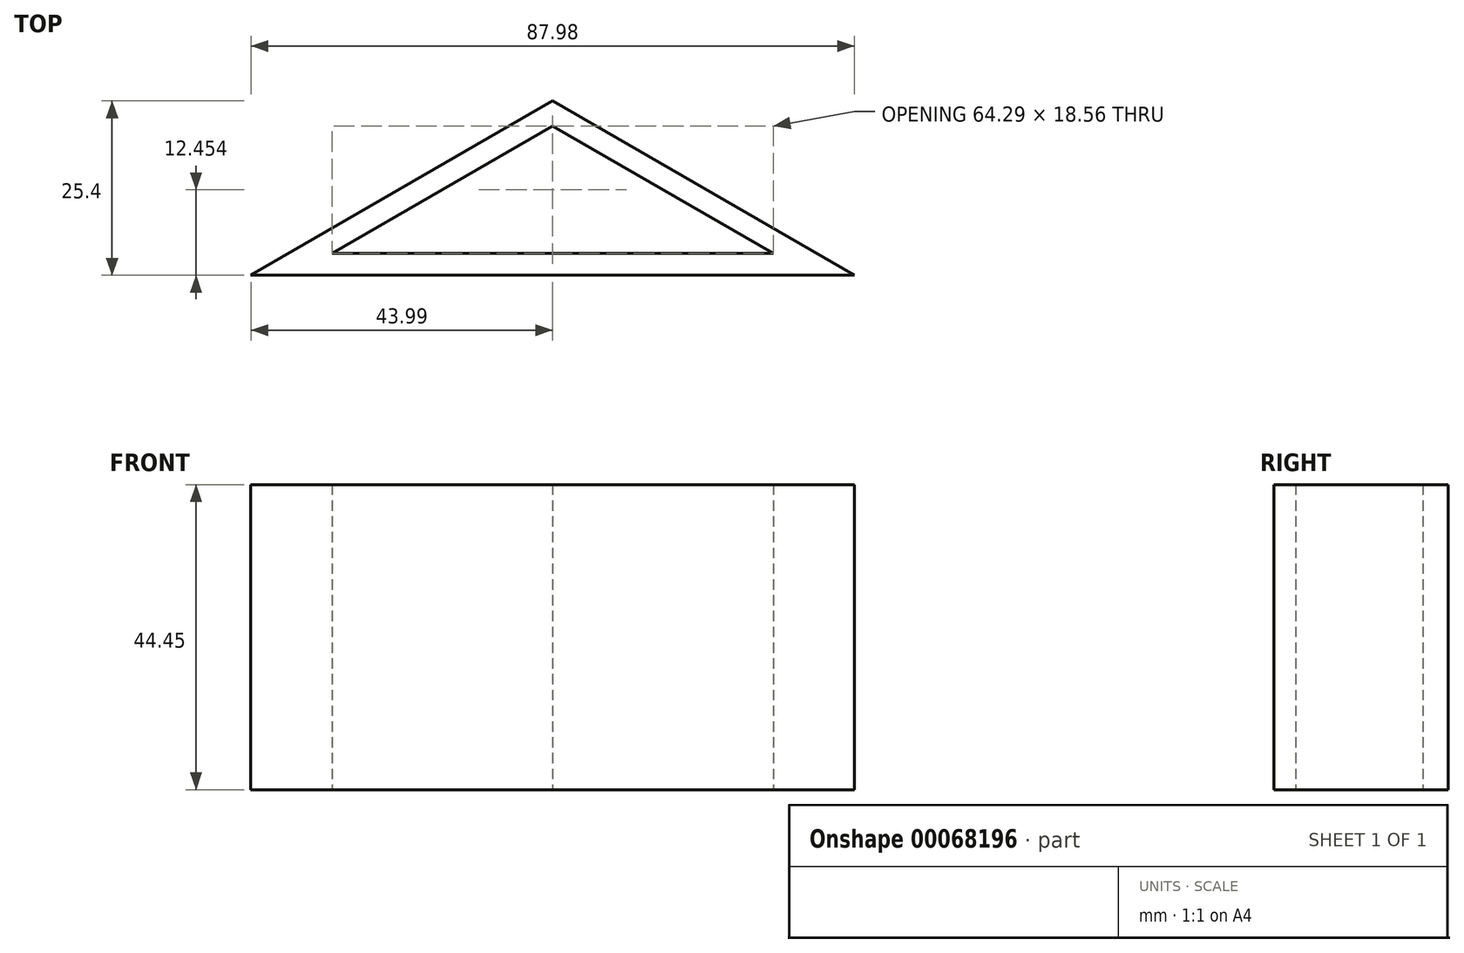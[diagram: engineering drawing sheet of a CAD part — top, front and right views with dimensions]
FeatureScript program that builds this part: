
annotation { "Feature Type Name" : "Feature", "Feature Type Description" : "" }
export const myFeature = defineFeature(function(context is Context, id is Id, definition is map)
    precondition{}
    {
        {
            var Q0;
            Q0=qCreatedBy(makeId("Top.planeOp"),FACE);
            var sketch = newSketch(context, id + "F0", { "sketchPlane" : qUnion([Q0])});
            skLineSegment(sketch, "E0", {"start": v(0, 25.4) * mm, "end": v(-44, 0) * mm});
            skLineSegment(sketch, "E1", {"start": v(-44, 0) * mm, "end": v(44, 0) * mm});
            skLineSegment(sketch, "E2", {"start": v(44, 0) * mm, "end": v(0, 25.4) * mm});
            skLineSegment(sketch, "E3.0", {"start": v(32.14, 3.17) * mm, "end": v(0, 21.73) * mm});
            skLineSegment(sketch, "E3.1", {"start": v(-32.14, 3.17) * mm, "end": v(32.14, 3.17) * mm});
            skLineSegment(sketch, "E3.2", {"start": v(0, 21.73) * mm, "end": v(-32.14, 3.17) * mm});
            skSolve(sketch);
        }
        {
            var Q0;
            Q0 = qSketchRegion(id + "F0", true);
            extrude(context, id + "F1", {"entities" : qUnion([Q0]), "depth" : 44.45 * mm});
        }
    });
